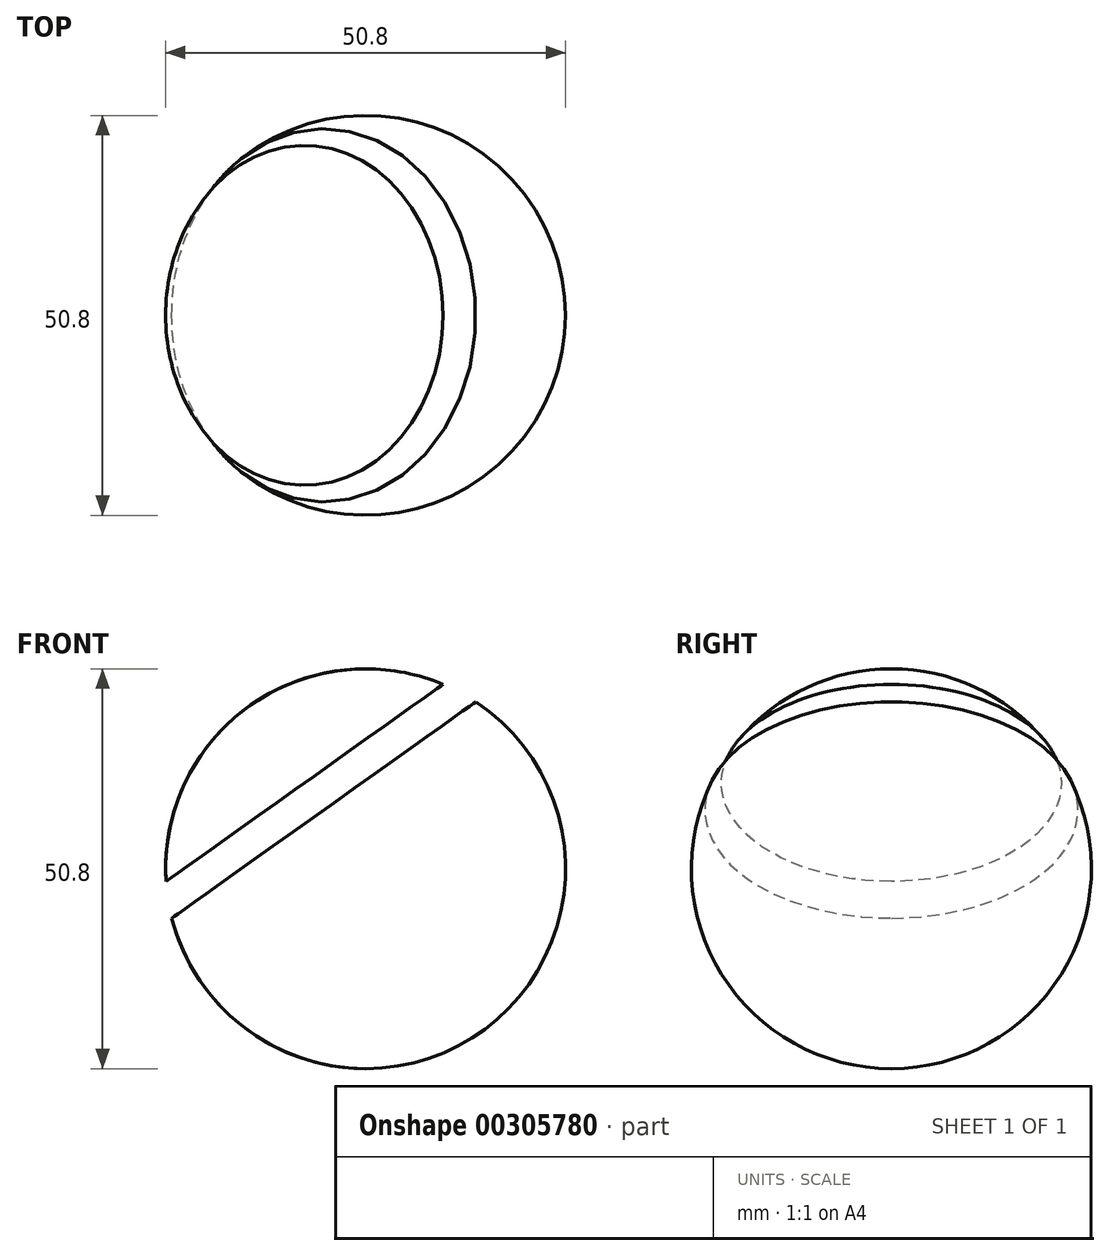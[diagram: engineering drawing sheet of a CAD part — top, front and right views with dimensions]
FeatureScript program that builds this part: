
annotation { "Feature Type Name" : "Feature", "Feature Type Description" : "" }
export const myFeature = defineFeature(function(context is Context, id is Id, definition is map)
    precondition{}
    {
        {
            var Q0;
            Q0=qCreatedBy(makeId("Front.planeOp"),FACE);
            var sketch = newSketch(context, id + "F0", { "sketchPlane" : qUnion([Q0])});
            skLineSegment(sketch, "E0", {"start": v(-50.8, 0) * mm, "end": v(-50.8, 50.8) * mm});
            skArc(sketch, "E1", {"start": v(-50.8, 0) * mm, "mid": v(-25.4, 25.4) * mm, "end": v(-50.8, 50.8) * mm});
            skSolve(sketch);
        }
        {
            var Q0;
            Q0 = qSketchRegion(id + "F0", true);
            var Q1;
            Q1=sQuery(id+"F0.wireOp",EDGE,"E0");
            revolve(context, id + "F1", {"entities" : qUnion([Q0]), "axis" : qUnion([Q1]), "revolveType" : RevolveType.FULL});
        }
        {
            var Q0;
            Q0=qCreatedBy(makeId("Front.planeOp"),FACE);
            var sketch = newSketch(context, id + "F2", { "sketchPlane" : qUnion([Q0])});
            skLineSegment(sketch, "E2", {"start": v(-82.12, 19.54) * mm, "end": v(-27.2, 58.62) * mm});
            skLineSegment(sketch, "E3", {"start": v(-27.2, 58.62) * mm, "end": v(-24.74, 55.17) * mm});
            skLineSegment(sketch, "E4", {"start": v(-24.74, 55.17) * mm, "end": v(-79.4, 16.28) * mm});
            skLineSegment(sketch, "E5", {"start": v(-79.4, 16.28) * mm, "end": v(-82.12, 19.54) * mm});
            skSolve(sketch);
        }
        {
            var Q0;
            Q0 = qSketchRegion(id + "F2", true);
            extrude(context, id + "F3", {"entities" : qUnion([Q0]), "operationType" : NewBodyOperationType.REMOVE, "depth" : 25.4 * mm, "hasSecondDirection" : true, "secondDirectionOppositeDirection" : true, "secondDirectionDepth" : 25.4 * mm});
        }
    });
